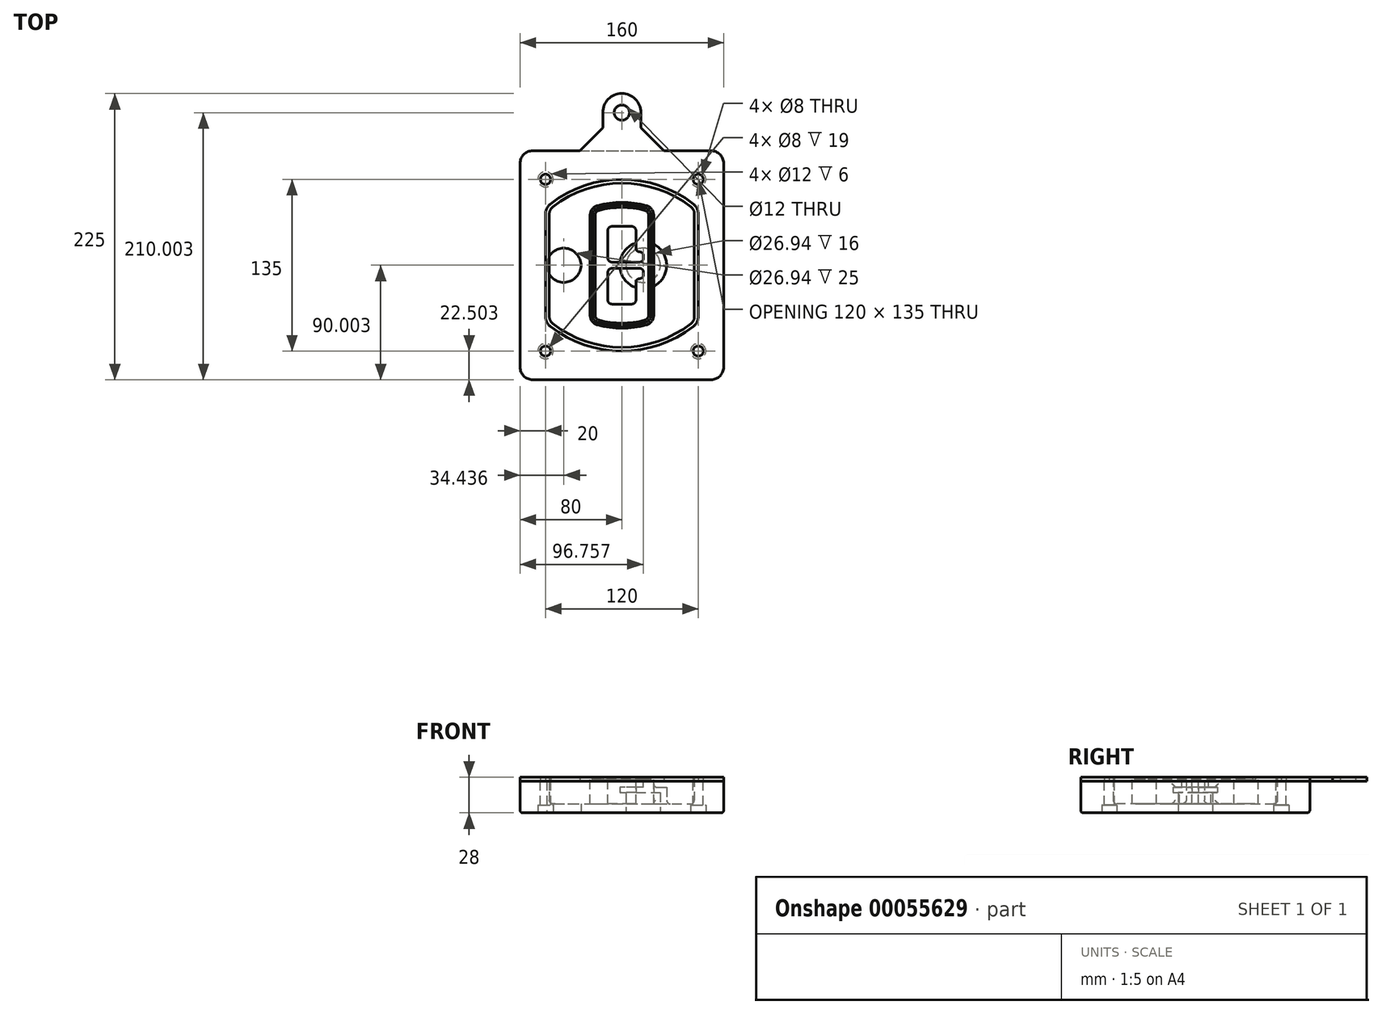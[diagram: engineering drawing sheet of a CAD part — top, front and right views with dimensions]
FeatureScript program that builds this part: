
annotation { "Feature Type Name" : "Feature", "Feature Type Description" : "" }
export const myFeature = defineFeature(function(context is Context, id is Id, definition is map)
    precondition{}
    {
        {
            var Q0;
            Q0=qCreatedBy(makeId("Top.planeOp"),FACE);
            var sketch = newSketch(context, id + "F0", { "sketchPlane" : qUnion([Q0])});
            skPoint(sketch, "E0.rect.middle", {"position": v(0, 0) * mm});
            skLineSegment(sketch, "E1.bottom", {"start": v(24.05, 28.38) * mm, "end": v(164.05, 28.38) * mm});
            skLineSegment(sketch, "E1.top", {"start": v(24.05, 208.38) * mm, "end": v(164.05, 208.38) * mm});
            skLineSegment(sketch, "E1.left", {"start": v(14.05, 38.38) * mm, "end": v(14.05, 198.38) * mm});
            skLineSegment(sketch, "E1.right", {"start": v(174.05, 38.38) * mm, "end": v(174.05, 198.38) * mm});
            skLineSegment(sketch, "E2", {"start": v(14.05, 208.38) * mm, "end": v(174.05, 28.38) * mm, "construction": true});
            skLineSegment(sketch, "E3", {"start": v(174.05, 208.38) * mm, "end": v(14.05, 28.38) * mm, "construction": true});
            skCircle(sketch, "E4", {"center": v(34.05, 185.88) * mm, "radius": 4 * mm});
            skCircle(sketch, "E5", {"center": v(154.05, 185.88) * mm, "radius": 4 * mm});
            skCircle(sketch, "E6", {"center": v(154.05, 50.88) * mm, "radius": 4 * mm});
            skCircle(sketch, "E7", {"center": v(34.05, 50.88) * mm, "radius": 4 * mm});
            skLineSegment(sketch, "E8", {"start": v(34.05, 185.88) * mm, "end": v(154.05, 185.88) * mm, "construction": true});
            skLineSegment(sketch, "E9", {"start": v(154.05, 185.88) * mm, "end": v(154.05, 50.88) * mm, "construction": true});
            skLineSegment(sketch, "E10", {"start": v(154.05, 50.88) * mm, "end": v(34.05, 50.88) * mm, "construction": true});
            skLineSegment(sketch, "E11", {"start": v(34.05, 50.88) * mm, "end": v(34.05, 185.88) * mm, "construction": true});
            skLineSegment(sketch, "E12", {"start": v(34.05, 158.68) * mm, "end": v(34.05, 78.09) * mm});
            skLineSegment(sketch, "E13", {"start": v(154.05, 158.68) * mm, "end": v(154.05, 78.09) * mm});
            skArc(sketch, "E14", {"start": v(150.2, 166.56) * mm, "mid": v(94.05, 185.88) * mm, "end": v(37.9, 166.56) * mm});
            skArc(sketch, "E15", {"start": v(37.9, 70.2) * mm, "mid": v(94.05, 50.88) * mm, "end": v(150.2, 70.2) * mm});
            skLineSegment(sketch, "E16", {"start": v(34.05, 118.38) * mm, "end": v(154.05, 118.38) * mm, "construction": true});
            skPoint(sketch, "E17.visualSharp", {"position": v(34.05, 73.38) * mm});
            skArc(sketch, "E17.filletArc", {"start": v(34.05, 78.09) * mm, "mid": v(35.06, 73.7) * mm, "end": v(37.9, 70.2) * mm});
            skPoint(sketch, "E18.visualSharp", {"position": v(34.05, 163.38) * mm});
            skArc(sketch, "E18.filletArc", {"start": v(37.9, 166.56) * mm, "mid": v(35.06, 163.06) * mm, "end": v(34.05, 158.68) * mm});
            skPoint(sketch, "E19.visualSharp", {"position": v(154.05, 163.38) * mm});
            skArc(sketch, "E19.filletArc", {"start": v(154.05, 158.68) * mm, "mid": v(153.04, 163.06) * mm, "end": v(150.2, 166.56) * mm});
            skPoint(sketch, "E20.visualSharp", {"position": v(154.05, 73.38) * mm});
            skArc(sketch, "E20.filletArc", {"start": v(150.2, 70.2) * mm, "mid": v(153.04, 73.7) * mm, "end": v(154.05, 78.09) * mm});
            skPoint(sketch, "E21.visualSharp", {"position": v(14.05, 208.38) * mm});
            skArc(sketch, "E21.filletArc", {"start": v(24.05, 208.38) * mm, "mid": v(16.98, 205.45) * mm, "end": v(14.05, 198.38) * mm});
            skPoint(sketch, "E22.visualSharp", {"position": v(174.05, 208.38) * mm});
            skArc(sketch, "E22.filletArc", {"start": v(174.05, 198.38) * mm, "mid": v(171.12, 205.45) * mm, "end": v(164.05, 208.38) * mm});
            skPoint(sketch, "E23.visualSharp", {"position": v(174.05, 28.38) * mm});
            skArc(sketch, "E23.filletArc", {"start": v(164.05, 28.38) * mm, "mid": v(171.12, 31.31) * mm, "end": v(174.05, 38.38) * mm});
            skPoint(sketch, "E24.visualSharp", {"position": v(14.05, 28.38) * mm});
            skArc(sketch, "E24.filletArc", {"start": v(14.05, 38.38) * mm, "mid": v(16.98, 31.31) * mm, "end": v(24.05, 28.38) * mm});
            skArc(sketch, "E25.0", {"start": v(151.05, 158.68) * mm, "mid": v(150.34, 161.75) * mm, "end": v(148.36, 164.2) * mm});
            skLineSegment(sketch, "E25.1", {"start": v(151.05, 158.68) * mm, "end": v(151.05, 78.09) * mm});
            skArc(sketch, "E25.2", {"start": v(148.36, 72.57) * mm, "mid": v(150.34, 75.02) * mm, "end": v(151.05, 78.09) * mm});
            skArc(sketch, "E25.3", {"start": v(39.74, 72.57) * mm, "mid": v(94.05, 53.88) * mm, "end": v(148.36, 72.57) * mm});
            skArc(sketch, "E25.4", {"start": v(37.05, 78.09) * mm, "mid": v(37.76, 75.02) * mm, "end": v(39.74, 72.57) * mm});
            skArc(sketch, "E25.5", {"start": v(148.36, 164.2) * mm, "mid": v(94.05, 182.88) * mm, "end": v(39.74, 164.2) * mm});
            skLineSegment(sketch, "E25.6", {"start": v(37.05, 158.68) * mm, "end": v(37.05, 78.09) * mm});
            skArc(sketch, "E25.7", {"start": v(39.74, 164.2) * mm, "mid": v(37.76, 161.75) * mm, "end": v(37.05, 158.68) * mm});
            skArc(sketch, "E26.0", {"start": v(35.43, 169.71) * mm, "mid": v(31.47, 164.82) * mm, "end": v(30.05, 158.68) * mm});
            skArc(sketch, "E26.1", {"start": v(152.67, 169.71) * mm, "mid": v(94.05, 189.88) * mm, "end": v(35.43, 169.71) * mm});
            skArc(sketch, "E26.2", {"start": v(158.05, 158.68) * mm, "mid": v(156.63, 164.82) * mm, "end": v(152.67, 169.71) * mm});
            skLineSegment(sketch, "E26.3", {"start": v(158.05, 158.68) * mm, "end": v(158.05, 78.09) * mm});
            skArc(sketch, "E26.4", {"start": v(152.67, 67.05) * mm, "mid": v(156.63, 71.95) * mm, "end": v(158.05, 78.09) * mm});
            skLineSegment(sketch, "E26.5", {"start": v(30.05, 158.68) * mm, "end": v(30.05, 78.09) * mm});
            skArc(sketch, "E26.6", {"start": v(35.43, 67.05) * mm, "mid": v(94.05, 46.88) * mm, "end": v(152.67, 67.05) * mm});
            skArc(sketch, "E26.7", {"start": v(30.05, 78.09) * mm, "mid": v(31.47, 71.95) * mm, "end": v(35.43, 67.05) * mm});
            skSolve(sketch);
        }
        {
            var Q0;
            Q0=makeQuery(id+"F0.imprint","IMPRINT",FACE,{"disambiguationData":[TD([[makeQuery(id+"F0.imprint","IMPRINT",EDGE,{"derivedFrom":sQuery(id+"F0.wireOp",EDGE,"E1.bottom")}),1.0]])]});
            var Q1;
            Q1=makeQuery(id+"F0.imprint","IMPRINT",FACE,{"disambiguationData":[TD([[makeQuery(id+"F0.imprint","IMPRINT",EDGE,{"derivedFrom":sQuery(id+"F0.wireOp",EDGE,"E12")}),1.0]])]});
            var Q2;
            Q2=makeQuery(id+"F0.imprint","IMPRINT",FACE,{"disambiguationData":[TD([[makeQuery(id+"F0.imprint","IMPRINT",EDGE,{"derivedFrom":sQuery(id+"F0.wireOp",EDGE,"E25.0")}),1.0]])]});
            var Q3;
            Q3=makeQuery(id+"F0.imprint","IMPRINT",FACE,{"disambiguationData":[TD([[makeQuery(id+"F0.imprint","IMPRINT",EDGE,{"derivedFrom":sQuery(id+"F0.wireOp",EDGE,"E12")}),-1.0]])]});
            extrude(context, id + "F1", {"entities" : qUnion([Q0, Q1, Q2, Q3]), "oppositeDirection" : true, "depth" : 25 * mm});
        }
        {
            var Q0;
            Q0=makeQuery(id+"F0.imprint","IMPRINT",FACE,{"disambiguationData":[TD([[makeQuery(id+"F0.imprint","IMPRINT",EDGE,{"derivedFrom":sQuery(id+"F0.wireOp",EDGE,"E12")}),1.0]])]});
            extrude(context, id + "F2", {"entities" : qUnion([Q0]), "operationType" : NewBodyOperationType.ADD, "depth" : 3 * mm});
        }
        {
            var Q0;
            Q0=makeQuery(id+"F0.imprint","IMPRINT",FACE,{"disambiguationData":[TD([[makeQuery(id+"F0.imprint","IMPRINT",EDGE,{"derivedFrom":sQuery(id+"F0.wireOp",EDGE,"E25.0")}),1.0]])]});
            extrude(context, id + "F3", {"entities" : qUnion([Q0]), "operationType" : NewBodyOperationType.REMOVE, "oppositeDirection" : true, "depth" : 18 * mm});
        }
        {
            var Q0;
            Q0=makeQuery(id+"F2.opExtrude","CAP_FACE",FACE,{"disambiguationData":[OSD([sQuery(id+"F0.wireOp",EDGE,"E12"),sQuery(id+"F0.wireOp",EDGE,"E13"),sQuery(id+"F0.wireOp",EDGE,"E14"),sQuery(id+"F0.wireOp",EDGE,"E15"),sQuery(id+"F0.wireOp",EDGE,"E17.filletArc"),sQuery(id+"F0.wireOp",EDGE,"E18.filletArc"),sQuery(id+"F0.wireOp",EDGE,"E19.filletArc"),sQuery(id+"F0.wireOp",EDGE,"E20.filletArc"),sQuery(id+"F0.wireOp",EDGE,"E25.0"),sQuery(id+"F0.wireOp",EDGE,"E25.1"),sQuery(id+"F0.wireOp",EDGE,"E25.2"),sQuery(id+"F0.wireOp",EDGE,"E25.3"),sQuery(id+"F0.wireOp",EDGE,"E25.4"),sQuery(id+"F0.wireOp",EDGE,"E25.5"),sQuery(id+"F0.wireOp",EDGE,"E25.6"),sQuery(id+"F0.wireOp",EDGE,"E25.7")])],"isStart":false});
            var sketch = newSketch(context, id + "F4", { "sketchPlane" : qUnion([Q0])});
            skArc(sketch, "E27.0", {"start": v(74.97, 71.41) * mm, "mid": v(94.05, 68.88) * mm, "end": v(113.13, 71.41) * mm});
            skArc(sketch, "E28.0", {"start": v(113.13, 165.35) * mm, "mid": v(94.05, 167.88) * mm, "end": v(74.97, 165.35) * mm});
            skLineSegment(sketch, "E29", {"start": v(69.05, 157.63) * mm, "end": v(69.05, 79.14) * mm});
            skLineSegment(sketch, "E30", {"start": v(119.05, 157.63) * mm, "end": v(119.05, 79.14) * mm});
            skLineSegment(sketch, "E31", {"start": v(69.05, 163.48) * mm, "end": v(119.05, 163.48) * mm, "construction": true});
            skLineSegment(sketch, "E32", {"start": v(69.05, 73.28) * mm, "end": v(119.05, 73.28) * mm, "construction": true});
            skPoint(sketch, "E33.visualSharp", {"position": v(69.05, 163.48) * mm});
            skArc(sketch, "E33.filletArc", {"start": v(74.97, 165.35) * mm, "mid": v(70.7, 162.5) * mm, "end": v(69.05, 157.63) * mm});
            skPoint(sketch, "E34.visualSharp", {"position": v(119.05, 163.48) * mm});
            skArc(sketch, "E34.filletArc", {"start": v(119.05, 157.63) * mm, "mid": v(117.4, 162.5) * mm, "end": v(113.13, 165.35) * mm});
            skPoint(sketch, "E35.visualSharp", {"position": v(119.05, 73.28) * mm});
            skArc(sketch, "E35.filletArc", {"start": v(113.13, 71.41) * mm, "mid": v(117.4, 74.27) * mm, "end": v(119.05, 79.14) * mm});
            skPoint(sketch, "E36.visualSharp", {"position": v(69.05, 73.28) * mm});
            skArc(sketch, "E36.filletArc", {"start": v(69.05, 79.14) * mm, "mid": v(70.7, 74.27) * mm, "end": v(74.97, 71.41) * mm});
            skArc(sketch, "E37.0", {"start": v(148.36, 164.2) * mm, "mid": v(94.05, 182.88) * mm, "end": v(39.74, 164.2) * mm});
            skArc(sketch, "E37.1", {"start": v(39.74, 164.2) * mm, "mid": v(37.76, 161.75) * mm, "end": v(37.05, 158.68) * mm});
            skLineSegment(sketch, "E37.2", {"start": v(37.05, 158.68) * mm, "end": v(37.05, 78.09) * mm});
            skArc(sketch, "E37.3", {"start": v(37.05, 78.09) * mm, "mid": v(37.76, 75.02) * mm, "end": v(39.74, 72.57) * mm});
            skArc(sketch, "E37.4", {"start": v(39.74, 72.57) * mm, "mid": v(94.05, 53.88) * mm, "end": v(148.36, 72.57) * mm});
            skArc(sketch, "E37.5", {"start": v(148.36, 72.57) * mm, "mid": v(150.34, 75.02) * mm, "end": v(151.05, 78.09) * mm});
            skLineSegment(sketch, "E37.6", {"start": v(151.05, 158.68) * mm, "end": v(151.05, 78.09) * mm});
            skArc(sketch, "E37.7", {"start": v(151.05, 158.68) * mm, "mid": v(150.34, 161.75) * mm, "end": v(148.36, 164.2) * mm});
            skLineSegment(sketch, "E38.0", {"start": v(117.05, 157.63) * mm, "end": v(117.05, 79.14) * mm});
            skArc(sketch, "E38.1", {"start": v(112.61, 73.34) * mm, "mid": v(115.81, 75.49) * mm, "end": v(117.05, 79.14) * mm});
            skArc(sketch, "E38.2", {"start": v(75.49, 73.34) * mm, "mid": v(94.05, 70.88) * mm, "end": v(112.61, 73.34) * mm});
            skArc(sketch, "E38.3", {"start": v(71.05, 79.14) * mm, "mid": v(72.29, 75.49) * mm, "end": v(75.49, 73.34) * mm});
            skLineSegment(sketch, "E38.4", {"start": v(71.05, 157.63) * mm, "end": v(71.05, 79.14) * mm});
            skArc(sketch, "E38.5", {"start": v(117.05, 157.63) * mm, "mid": v(115.81, 161.28) * mm, "end": v(112.61, 163.42) * mm});
            skArc(sketch, "E38.6", {"start": v(75.49, 163.42) * mm, "mid": v(72.29, 161.28) * mm, "end": v(71.05, 157.63) * mm});
            skArc(sketch, "E38.7", {"start": v(112.61, 163.42) * mm, "mid": v(94.05, 165.88) * mm, "end": v(75.49, 163.42) * mm});
            skArc(sketch, "E39.0", {"start": v(115.05, 157.63) * mm, "mid": v(114.23, 160.06) * mm, "end": v(112.1, 161.5) * mm});
            skLineSegment(sketch, "E39.1", {"start": v(115.05, 157.63) * mm, "end": v(115.05, 79.14) * mm});
            skArc(sketch, "E39.2", {"start": v(112.1, 75.27) * mm, "mid": v(114.23, 76.7) * mm, "end": v(115.05, 79.14) * mm});
            skArc(sketch, "E39.3", {"start": v(76, 75.27) * mm, "mid": v(94.05, 72.88) * mm, "end": v(112.1, 75.27) * mm});
            skArc(sketch, "E39.4", {"start": v(73.05, 79.14) * mm, "mid": v(73.87, 76.7) * mm, "end": v(76, 75.27) * mm});
            skArc(sketch, "E39.5", {"start": v(112.1, 161.5) * mm, "mid": v(94.05, 163.88) * mm, "end": v(76, 161.5) * mm});
            skLineSegment(sketch, "E39.6", {"start": v(73.05, 157.63) * mm, "end": v(73.05, 79.14) * mm});
            skArc(sketch, "E39.7", {"start": v(76, 161.5) * mm, "mid": v(73.87, 160.06) * mm, "end": v(73.05, 157.63) * mm});
            skLineSegment(sketch, "E40", {"start": v(69.05, 118.38) * mm, "end": v(119.05, 118.38) * mm, "construction": true});
            skLineSegment(sketch, "E41", {"start": v(83.05, 123.88) * mm, "end": v(83.05, 145.88) * mm});
            skLineSegment(sketch, "E42", {"start": v(86.05, 148.88) * mm, "end": v(102.05, 148.88) * mm});
            skLineSegment(sketch, "E43", {"start": v(105.05, 145.88) * mm, "end": v(105.05, 131.88) * mm});
            skLineSegment(sketch, "E44", {"start": v(108.05, 128.88) * mm, "end": v(108.05, 128.88) * mm});
            skLineSegment(sketch, "E45", {"start": v(111.05, 125.88) * mm, "end": v(111.05, 123.88) * mm});
            skLineSegment(sketch, "E46", {"start": v(108.05, 120.88) * mm, "end": v(86.05, 120.88) * mm});
            skPoint(sketch, "E47.visualSharp", {"position": v(83.05, 148.88) * mm});
            skArc(sketch, "E47.filletArc", {"start": v(86.05, 148.88) * mm, "mid": v(83.93, 148) * mm, "end": v(83.05, 145.88) * mm});
            skPoint(sketch, "E48.visualSharp", {"position": v(105.05, 148.88) * mm});
            skArc(sketch, "E48.filletArc", {"start": v(105.05, 145.88) * mm, "mid": v(104.17, 148) * mm, "end": v(102.05, 148.88) * mm});
            skPoint(sketch, "E49.visualSharp", {"position": v(105.05, 128.88) * mm});
            skArc(sketch, "E49.filletArc", {"start": v(105.05, 131.88) * mm, "mid": v(105.93, 129.76) * mm, "end": v(108.05, 128.88) * mm});
            skPoint(sketch, "E50.visualSharp", {"position": v(111.05, 128.88) * mm});
            skArc(sketch, "E50.filletArc", {"start": v(111.05, 125.88) * mm, "mid": v(110.17, 128) * mm, "end": v(108.05, 128.88) * mm});
            skPoint(sketch, "E51.visualSharp", {"position": v(111.05, 120.88) * mm});
            skArc(sketch, "E51.filletArc", {"start": v(108.05, 120.88) * mm, "mid": v(110.17, 121.76) * mm, "end": v(111.05, 123.88) * mm});
            skPoint(sketch, "E52.visualSharp", {"position": v(83.05, 120.88) * mm});
            skArc(sketch, "E52.filletArc", {"start": v(83.05, 123.88) * mm, "mid": v(83.93, 121.76) * mm, "end": v(86.05, 120.88) * mm});
            skLineSegment(sketch, "E53.0.MirrorCS", {"start": v(108.05, 115.88) * mm, "end": v(86.05, 115.88) * mm});
            skArc(sketch, "E54.0.MirrorCS", {"start": v(83.05, 112.88) * mm, "mid": v(83.93, 115) * mm, "end": v(86.05, 115.88) * mm});
            skLineSegment(sketch, "E55.0.MirrorCS", {"start": v(83.05, 112.88) * mm, "end": v(83.05, 90.88) * mm});
            skArc(sketch, "E56.0.MirrorCS", {"start": v(86.05, 87.88) * mm, "mid": v(83.93, 88.76) * mm, "end": v(83.05, 90.88) * mm});
            skLineSegment(sketch, "E57.0.MirrorCS", {"start": v(86.05, 87.88) * mm, "end": v(102.05, 87.88) * mm});
            skArc(sketch, "E58.0.MirrorCS", {"start": v(105.05, 90.88) * mm, "mid": v(104.17, 88.76) * mm, "end": v(102.05, 87.88) * mm});
            skLineSegment(sketch, "E59.0.MirrorCS", {"start": v(105.05, 90.88) * mm, "end": v(105.05, 104.88) * mm});
            skArc(sketch, "E60.0.MirrorCS", {"start": v(105.05, 104.88) * mm, "mid": v(105.93, 107) * mm, "end": v(108.05, 107.88) * mm});
            skArc(sketch, "E61.0.MirrorCS", {"start": v(111.05, 110.88) * mm, "mid": v(110.17, 108.76) * mm, "end": v(108.05, 107.88) * mm});
            skLineSegment(sketch, "E62.0.MirrorCS", {"start": v(111.05, 110.88) * mm, "end": v(111.05, 112.88) * mm});
            skArc(sketch, "E63.0.MirrorCS", {"start": v(108.05, 115.88) * mm, "mid": v(110.17, 115) * mm, "end": v(111.05, 112.88) * mm});
            skSolve(sketch);
        }
        {
            var Q0;
            Q0=makeQuery(id+"F4.imprint","IMPRINT",FACE,{"disambiguationData":[TD([[makeQuery(id+"F4.imprint","IMPRINT",EDGE,{"derivedFrom":sQuery(id+"F4.wireOp",EDGE,"E27.0")}),1.0]])]});
            var Q1;
            Q1=makeQuery(id+"F4.imprint","IMPRINT",FACE,{"disambiguationData":[TD([[makeQuery(id+"F4.imprint","IMPRINT",EDGE,{"derivedFrom":sQuery(id+"F4.wireOp",EDGE,"E38.0")}),-1.0]])]});
            var Q2;
            Q2=makeQuery(id+"F4.imprint","IMPRINT",FACE,{"disambiguationData":[TD([[makeQuery(id+"F4.imprint","IMPRINT",EDGE,{"derivedFrom":sQuery(id+"F4.wireOp",EDGE,"E39.0")}),1.0]])]});
            extrude(context, id + "F5", {"entities" : qUnion([Q0, Q1, Q2]), "operationType" : NewBodyOperationType.ADD, "endBound" : BoundingType.UP_TO_NEXT, "oppositeDirection" : true, "depth" : 25 * mm});
        }
        {
            var Q0;
            Q0=makeQuery(id+"F4.imprint","IMPRINT",FACE,{"disambiguationData":[TD([[makeQuery(id+"F4.imprint","IMPRINT",EDGE,{"derivedFrom":sQuery(id+"F4.wireOp",EDGE,"E38.0")}),-1.0]])]});
            extrude(context, id + "F6", {"entities" : qUnion([Q0]), "operationType" : NewBodyOperationType.REMOVE, "oppositeDirection" : true, "depth" : 2 * mm});
        }
        {
            var Q0;
            Q0=makeQuery(id+"F1.opExtrude","CAP_FACE",FACE,{"disambiguationData":[OSD([sQuery(id+"F0.wireOp",EDGE,"E1.bottom"),sQuery(id+"F0.wireOp",EDGE,"E1.top"),sQuery(id+"F0.wireOp",EDGE,"E1.left"),sQuery(id+"F0.wireOp",EDGE,"E1.right"),sQuery(id+"F0.wireOp",EDGE,"E4"),sQuery(id+"F0.wireOp",EDGE,"E5"),sQuery(id+"F0.wireOp",EDGE,"E6"),sQuery(id+"F0.wireOp",EDGE,"E7"),sQuery(id+"F0.wireOp",EDGE,"E21.filletArc"),sQuery(id+"F0.wireOp",EDGE,"E22.filletArc"),sQuery(id+"F0.wireOp",EDGE,"E23.filletArc"),sQuery(id+"F0.wireOp",EDGE,"E24.filletArc")])],"isStart":false});
            var sketch = newSketch(context, id + "F7", { "sketchPlane" : qUnion([Q0])});
            skCircle(sketch, "E64", {"center": v(110.8, -118.38) * mm, "radius": 13.47 * mm});
            skCircle(sketch, "E65", {"center": v(48.49, -118.38) * mm, "radius": 13.47 * mm});
            skLineSegment(sketch, "E66", {"start": v(174.05, -118.38) * mm, "end": v(14.05, -118.38) * mm});
            skCircle(sketch, "E67", {"center": v(110.8, -118.38) * mm, "radius": 18.47 * mm});
            skCircle(sketch, "E68", {"center": v(154.05, -185.88) * mm, "radius": 6 * mm});
            skCircle(sketch, "E69", {"center": v(34.05, -185.88) * mm, "radius": 6 * mm});
            skCircle(sketch, "E70", {"center": v(34.05, -50.88) * mm, "radius": 6 * mm});
            skCircle(sketch, "E71", {"center": v(154.05, -50.88) * mm, "radius": 6 * mm});
            skSolve(sketch);
        }
        {
            var Q0;
            {var subQ1=sQuery(id+"F7.wireOp",EDGE,"E66");var subQ4=sQuery(id+"F7.wireOp",EDGE,"E64");var subQ6=makeQuery(id+"F7.imprint","INTERSECT",VERTEX,{"disambiguationData":[OD(0.0)],"derivedFrom":[subQ4,subQ1]});Q0=makeQuery(id+"F7.imprint","IMPRINT",FACE,{"disambiguationData":[TD([[makeQuery(id+"F7.imprint","IMPRINT",EDGE,{"disambiguationData":[TD([[subQ6,-1.0]])],"derivedFrom":subQ4}),-1.0]])]});}
            var Q1;
            {var subQ0=sQuery(id+"F7.wireOp",EDGE,"E66");var subQ1=sQuery(id+"F7.wireOp",EDGE,"E64");var subQ3=makeQuery(id+"F7.imprint","INTERSECT",VERTEX,{"disambiguationData":[OD(0.0)],"derivedFrom":[subQ1,subQ0]});Q1=makeQuery(id+"F7.imprint","IMPRINT",FACE,{"disambiguationData":[TD([[makeQuery(id+"F7.imprint","IMPRINT",EDGE,{"disambiguationData":[TD([[subQ3,-1.0]])],"derivedFrom":subQ1}),1.0]])]});}
            var Q2;
            {var subQ0=sQuery(id+"F7.wireOp",EDGE,"E66");var subQ1=sQuery(id+"F7.wireOp",EDGE,"E64");var subQ3=makeQuery(id+"F7.imprint","INTERSECT",VERTEX,{"disambiguationData":[OD(0.0)],"derivedFrom":[subQ1,subQ0]});Q2=makeQuery(id+"F7.imprint","IMPRINT",FACE,{"disambiguationData":[TD([[makeQuery(id+"F7.imprint","IMPRINT",EDGE,{"disambiguationData":[TD([[subQ3,1.0]])],"derivedFrom":subQ1}),1.0]])]});}
            var Q3;
            {var subQ1=sQuery(id+"F7.wireOp",EDGE,"E66");var subQ4=sQuery(id+"F7.wireOp",EDGE,"E64");var subQ6=makeQuery(id+"F7.imprint","INTERSECT",VERTEX,{"disambiguationData":[OD(0.0)],"derivedFrom":[subQ4,subQ1]});Q3=makeQuery(id+"F7.imprint","IMPRINT",FACE,{"disambiguationData":[TD([[makeQuery(id+"F7.imprint","IMPRINT",EDGE,{"disambiguationData":[TD([[subQ6,1.0]])],"derivedFrom":subQ4}),-1.0]])]});}
            extrude(context, id + "F8", {"entities" : qUnion([Q0, Q1, Q2, Q3]), "operationType" : NewBodyOperationType.ADD, "oppositeDirection" : true, "depth" : 20 * mm});
        }
        {
            var Q0;
            {var subQ0=sQuery(id+"F7.wireOp",EDGE,"E66");var subQ1=sQuery(id+"F7.wireOp",EDGE,"E64");var subQ3=makeQuery(id+"F7.imprint","INTERSECT",VERTEX,{"disambiguationData":[OD(0.0)],"derivedFrom":[subQ1,subQ0]});Q0=makeQuery(id+"F7.imprint","IMPRINT",FACE,{"disambiguationData":[TD([[makeQuery(id+"F7.imprint","IMPRINT",EDGE,{"disambiguationData":[TD([[subQ3,-1.0]])],"derivedFrom":subQ1}),1.0]])]});}
            var Q1;
            {var subQ0=sQuery(id+"F7.wireOp",EDGE,"E66");var subQ1=sQuery(id+"F7.wireOp",EDGE,"E64");var subQ3=makeQuery(id+"F7.imprint","INTERSECT",VERTEX,{"disambiguationData":[OD(0.0)],"derivedFrom":[subQ1,subQ0]});Q1=makeQuery(id+"F7.imprint","IMPRINT",FACE,{"disambiguationData":[TD([[makeQuery(id+"F7.imprint","IMPRINT",EDGE,{"disambiguationData":[TD([[subQ3,1.0]])],"derivedFrom":subQ1}),1.0]])]});}
            extrude(context, id + "F9", {"entities" : qUnion([Q0, Q1]), "operationType" : NewBodyOperationType.REMOVE, "oppositeDirection" : true, "depth" : 16 * mm});
        }
        {
            var Q0;
            {var subQ0=sQuery(id+"F7.wireOp",EDGE,"E66");var subQ1=sQuery(id+"F7.wireOp",EDGE,"E65");var subQ3=makeQuery(id+"F7.imprint","INTERSECT",VERTEX,{"disambiguationData":[OD(0.0)],"derivedFrom":[subQ1,subQ0]});Q0=makeQuery(id+"F7.imprint","IMPRINT",FACE,{"disambiguationData":[TD([[makeQuery(id+"F7.imprint","IMPRINT",EDGE,{"disambiguationData":[TD([[subQ3,-1.0]])],"derivedFrom":subQ1}),1.0]])]});}
            var Q1;
            {var subQ0=sQuery(id+"F7.wireOp",EDGE,"E66");var subQ1=sQuery(id+"F7.wireOp",EDGE,"E65");var subQ3=makeQuery(id+"F7.imprint","INTERSECT",VERTEX,{"disambiguationData":[OD(0.0)],"derivedFrom":[subQ1,subQ0]});Q1=makeQuery(id+"F7.imprint","IMPRINT",FACE,{"disambiguationData":[TD([[makeQuery(id+"F7.imprint","IMPRINT",EDGE,{"disambiguationData":[TD([[subQ3,1.0]])],"derivedFrom":subQ1}),1.0]])]});}
            extrude(context, id + "F10", {"entities" : qUnion([Q0, Q1]), "operationType" : NewBodyOperationType.REMOVE, "oppositeDirection" : true, "depth" : 25 * mm});
        }
        {
            var Q0;
            Q0=makeQuery(id+"F7.imprint","IMPRINT",FACE,{"disambiguationData":[TD([[makeQuery(id+"F7.imprint","IMPRINT",EDGE,{"derivedFrom":sQuery(id+"F7.wireOp",EDGE,"E68")}),1.0]])]});
            var Q1;
            Q1=makeQuery(id+"F7.imprint","IMPRINT",FACE,{"disambiguationData":[TD([[makeQuery(id+"F7.imprint","IMPRINT",EDGE,{"derivedFrom":makeQuery(id+"F1.opExtrude","CAP_EDGE",EDGE,{"disambiguationData":[OSD([sQuery(id+"F0.wireOp",EDGE,"E5")])],"isStart":false})}),-1.0]])]});
            var Q2;
            Q2=makeQuery(id+"F7.imprint","IMPRINT",FACE,{"disambiguationData":[TD([[makeQuery(id+"F7.imprint","IMPRINT",EDGE,{"derivedFrom":sQuery(id+"F7.wireOp",EDGE,"E69")}),1.0]])]});
            var Q3;
            Q3=makeQuery(id+"F7.imprint","IMPRINT",FACE,{"disambiguationData":[TD([[makeQuery(id+"F7.imprint","IMPRINT",EDGE,{"derivedFrom":makeQuery(id+"F1.opExtrude","CAP_EDGE",EDGE,{"disambiguationData":[OSD([sQuery(id+"F0.wireOp",EDGE,"E4")])],"isStart":false})}),-1.0]])]});
            var Q4;
            Q4=makeQuery(id+"F7.imprint","IMPRINT",FACE,{"disambiguationData":[TD([[makeQuery(id+"F7.imprint","IMPRINT",EDGE,{"derivedFrom":sQuery(id+"F7.wireOp",EDGE,"E70")}),1.0]])]});
            var Q5;
            Q5=makeQuery(id+"F7.imprint","IMPRINT",FACE,{"disambiguationData":[TD([[makeQuery(id+"F7.imprint","IMPRINT",EDGE,{"derivedFrom":makeQuery(id+"F1.opExtrude","CAP_EDGE",EDGE,{"disambiguationData":[OSD([sQuery(id+"F0.wireOp",EDGE,"E7")])],"isStart":false})}),-1.0]])]});
            var Q6;
            Q6=makeQuery(id+"F7.imprint","IMPRINT",FACE,{"disambiguationData":[TD([[makeQuery(id+"F7.imprint","IMPRINT",EDGE,{"derivedFrom":sQuery(id+"F7.wireOp",EDGE,"E71")}),1.0]])]});
            var Q7;
            Q7=makeQuery(id+"F7.imprint","IMPRINT",FACE,{"disambiguationData":[TD([[makeQuery(id+"F7.imprint","IMPRINT",EDGE,{"derivedFrom":makeQuery(id+"F1.opExtrude","CAP_EDGE",EDGE,{"disambiguationData":[OSD([sQuery(id+"F0.wireOp",EDGE,"E6")])],"isStart":false})}),-1.0]])]});
            extrude(context, id + "F11", {"entities" : qUnion([Q0, Q1, Q2, Q3, Q4, Q5, Q6, Q7]), "operationType" : NewBodyOperationType.REMOVE, "oppositeDirection" : true, "depth" : 6 * mm});
        }
        {
            var Q0;
            Q0=makeQuery(id+"F9.boolean.opBoolean","COPY",FACE,{"derivedFrom":makeQuery(id+"F9.opExtrude","CAP_FACE",FACE,{"disambiguationData":[OSD([sQuery(id+"F7.wireOp",EDGE,"E64")])],"isStart":false})});
            var sketch = newSketch(context, id + "F12", { "sketchPlane" : qUnion([Q0])});
            skArc(sketch, "E72.0", {"start": v(105.05, -100.83) * mm, "mid": v(96.62, -106.56) * mm, "end": v(92.5, -115.88) * mm});
            skArc(sketch, "E72.1", {"start": v(92.5, -120.88) * mm, "mid": v(96.62, -130.2) * mm, "end": v(105.05, -135.93) * mm});
            skLineSegment(sketch, "E73", {"start": v(92.5, -120.88) * mm, "end": v(108.05, -120.88) * mm});
            skLineSegment(sketch, "E74.0", {"start": v(108.05, -115.88) * mm, "end": v(92.5, -115.88) * mm});
            skArc(sketch, "E74.1", {"start": v(108.05, -115.88) * mm, "mid": v(110.17, -115) * mm, "end": v(111.05, -112.88) * mm});
            skLineSegment(sketch, "E74.2", {"start": v(111.05, -110.88) * mm, "end": v(111.05, -112.88) * mm});
            skArc(sketch, "E74.3", {"start": v(111.05, -110.88) * mm, "mid": v(110.17, -108.76) * mm, "end": v(108.05, -107.88) * mm});
            skArc(sketch, "E74.4", {"start": v(105.05, -104.88) * mm, "mid": v(105.93, -107) * mm, "end": v(108.05, -107.88) * mm});
            skLineSegment(sketch, "E74.5", {"start": v(105.05, -100.83) * mm, "end": v(105.05, -104.88) * mm});
            skLineSegment(sketch, "E74.7", {"start": v(108.05, -120.88) * mm, "end": v(92.5, -120.88) * mm});
            skArc(sketch, "E74.8", {"start": v(108.05, -120.88) * mm, "mid": v(110.17, -121.76) * mm, "end": v(111.05, -123.88) * mm});
            skLineSegment(sketch, "E74.9", {"start": v(111.05, -125.88) * mm, "end": v(111.05, -123.88) * mm});
            skArc(sketch, "E74.10", {"start": v(111.05, -125.88) * mm, "mid": v(110.17, -128) * mm, "end": v(108.05, -128.88) * mm});
            skArc(sketch, "E74.11", {"start": v(105.05, -131.88) * mm, "mid": v(105.93, -129.76) * mm, "end": v(108.05, -128.88) * mm});
            skLineSegment(sketch, "E74.12", {"start": v(105.05, -135.93) * mm, "end": v(105.05, -131.88) * mm});
            skPoint(sketch, "E75.orphan", {"position": v(105.05, -145.88) * mm});
            skPoint(sketch, "E76.orphan", {"position": v(86.05, -120.88) * mm});
            skPoint(sketch, "E77.orphan", {"position": v(86.05, -115.88) * mm});
            skPoint(sketch, "E78.orphan", {"position": v(105.05, -90.88) * mm});
            skSolve(sketch);
        }
        {
            var Q0;
            {var subQ7=sQuery(id+"F12.wireOp",EDGE,"E72.0");var subQ14=sQuery(id+"F12.wireOp",EDGE,"E72.1");var subQ16=sQuery(id+"F12.wireOp",EDGE,"E74.1");var subQ18=sQuery(id+"F12.wireOp",EDGE,"E74.8");Q0=qUnion([makeQuery(id+"F12.imprint","IMPRINT",FACE,{"disambiguationData":[TD([[makeQuery(id+"F12.imprint","IMPRINT",EDGE,{"derivedFrom":subQ7}),1.0]])]}),makeQuery(id+"F12.imprint","IMPRINT",FACE,{"disambiguationData":[TD([[makeQuery(id+"F12.imprint","IMPRINT",EDGE,{"derivedFrom":subQ14}),1.0]])]}),makeQuery(id+"F12.imprint","IMPRINT",FACE,{"disambiguationData":[TD([[makeQuery(id+"F12.imprint","IMPRINT",EDGE,{"derivedFrom":subQ16}),1.0]])]}),makeQuery(id+"F12.imprint","IMPRINT",FACE,{"disambiguationData":[TD([[makeQuery(id+"F12.imprint","IMPRINT",EDGE,{"derivedFrom":subQ18}),-1.0]])]})]);}
            var Q1;
            Q1=makeQuery(id+"F5.boolean.opBoolean","SPLIT",FACE,{"disambiguationData":[TD([makeQuery(id+"F5.opExtrude","SWEPT_FACE",FACE,{"disambiguationData":[OSD([sQuery(id+"F4.wireOp",EDGE,"E41")])]})])],"derivedFrom":makeQuery(id+"F3.boolean.opBoolean","COPY",FACE,{"derivedFrom":makeQuery(id+"F3.opExtrude","CAP_FACE",FACE,{"disambiguationData":[OSD([sQuery(id+"F0.wireOp",EDGE,"E25.0"),sQuery(id+"F0.wireOp",EDGE,"E25.1"),sQuery(id+"F0.wireOp",EDGE,"E25.2"),sQuery(id+"F0.wireOp",EDGE,"E25.3"),sQuery(id+"F0.wireOp",EDGE,"E25.4"),sQuery(id+"F0.wireOp",EDGE,"E25.5"),sQuery(id+"F0.wireOp",EDGE,"E25.6"),sQuery(id+"F0.wireOp",EDGE,"E25.7")])],"isStart":false})})});
            extrude(context, id + "F13", {"entities" : qUnion([Q0]), "operationType" : NewBodyOperationType.REMOVE, "endBound" : BoundingType.UP_TO_SURFACE, "endBoundEntityFace" : qUnion([Q1]), "depth" : 25 * mm});
        }
        {
            var Q0;
            Q0=makeQuery(id+"F3.boolean.opBoolean","COPY",EDGE,{"derivedFrom":makeQuery(id+"F3.opExtrude","CAP_EDGE",EDGE,{"disambiguationData":[OSD([sQuery(id+"F0.wireOp",EDGE,"E25.6")])],"isStart":false})});
            var Q1;
            Q1=makeQuery(id+"F8.boolean.opBoolean","INTERSECT",EDGE,{"derivedFrom":[makeQuery(id+"F5.opExtrude","SWEPT_FACE",FACE,{"disambiguationData":[OSD([sQuery(id+"F4.wireOp",EDGE,"E30")])]}),makeQuery(id+"F8.opExtrude","CAP_FACE",FACE,{"disambiguationData":[OSD([sQuery(id+"F7.wireOp",EDGE,"E67")])],"isStart":false})]});
            var Q2;
            Q2=makeQuery(id+"F8.boolean.opBoolean","INTERSECT",EDGE,{"disambiguationData":[OD(1.0)],"derivedFrom":[makeQuery(id+"F5.opExtrude","SWEPT_FACE",FACE,{"disambiguationData":[OSD([sQuery(id+"F4.wireOp",EDGE,"E30")])]}),makeQuery(id+"F8.opExtrude","SWEPT_FACE",FACE,{"disambiguationData":[OSD([sQuery(id+"F7.wireOp",EDGE,"E67")])]})]});
            var Q3;
            {var subQ0=makeQuery(id+"F3.boolean.opBoolean","COPY",FACE,{"derivedFrom":makeQuery(id+"F3.opExtrude","CAP_FACE",FACE,{"disambiguationData":[OSD([sQuery(id+"F0.wireOp",EDGE,"E25.0"),sQuery(id+"F0.wireOp",EDGE,"E25.1"),sQuery(id+"F0.wireOp",EDGE,"E25.2"),sQuery(id+"F0.wireOp",EDGE,"E25.3"),sQuery(id+"F0.wireOp",EDGE,"E25.4"),sQuery(id+"F0.wireOp",EDGE,"E25.5"),sQuery(id+"F0.wireOp",EDGE,"E25.6"),sQuery(id+"F0.wireOp",EDGE,"E25.7")])],"isStart":false})});var subQ1=sQuery(id+"F4.wireOp",EDGE,"E30");Q3=makeQuery(id+"F8.boolean.opBoolean","SPLIT",EDGE,{"disambiguationData":[TD([makeQuery(id+"F5.opExtrude","SWEPT_FACE",FACE,{"disambiguationData":[OSD([sQuery(id+"F4.wireOp",EDGE,"E35.filletArc")])]})])],"derivedFrom":makeQuery(id+"F5.opExtrude","TWEAK_EDGE",EDGE,{"derivedFrom":[subQ0,makeQuery(id+"F4.imprint","IMPRINT",EDGE,{"derivedFrom":subQ1})]})});}
            var Q4;
            {var subQ0=sQuery(id+"F0.wireOp",EDGE,"E25.0");var subQ1=sQuery(id+"F0.wireOp",EDGE,"E25.1");var subQ2=sQuery(id+"F0.wireOp",EDGE,"E25.2");var subQ3=sQuery(id+"F0.wireOp",EDGE,"E25.3");var subQ4=sQuery(id+"F0.wireOp",EDGE,"E25.4");var subQ5=sQuery(id+"F0.wireOp",EDGE,"E25.5");var subQ6=sQuery(id+"F0.wireOp",EDGE,"E25.6");var subQ7=sQuery(id+"F0.wireOp",EDGE,"E25.7");Q4=makeQuery(id+"F8.boolean.opBoolean","INTERSECT",EDGE,{"derivedFrom":[makeQuery(id+"F5.boolean.opBoolean","SPLIT",FACE,{"disambiguationData":[TD([makeQuery(id+"F2.opExtrude","SWEPT_FACE",FACE,{"disambiguationData":[OSD([subQ0])]})])],"derivedFrom":makeQuery(id+"F3.boolean.opBoolean","COPY",FACE,{"derivedFrom":makeQuery(id+"F3.opExtrude","CAP_FACE",FACE,{"disambiguationData":[OSD([subQ0,subQ1,subQ2,subQ3,subQ4,subQ5,subQ6,subQ7])],"isStart":false})})}),makeQuery(id+"F8.opExtrude","SWEPT_FACE",FACE,{"disambiguationData":[OSD([sQuery(id+"F7.wireOp",EDGE,"E67")])]})]});}
            var Q5;
            Q5=makeQuery(id+"F8.boolean.opBoolean","INTERSECT",EDGE,{"disambiguationData":[OD(0.0)],"derivedFrom":[makeQuery(id+"F5.opExtrude","SWEPT_FACE",FACE,{"disambiguationData":[OSD([sQuery(id+"F4.wireOp",EDGE,"E30")])]}),makeQuery(id+"F8.opExtrude","SWEPT_FACE",FACE,{"disambiguationData":[OSD([sQuery(id+"F7.wireOp",EDGE,"E67")])]})]});
            fillet(context, id + "F14", {"entities" : qUnion([Q0, Q1, Q2, Q3, Q4, Q5]), "radius" : 3 * mm, "tangentPropagation" : true, "allowEdgeOverflow" : false});
        }
        {
            var Q0;
            Q0=makeQuery(id+"F1.opExtrude","CAP_EDGE",EDGE,{"disambiguationData":[OSD([sQuery(id+"F0.wireOp",EDGE,"E1.bottom")])],"isStart":false});
            fillet(context, id + "F15", {"entities" : qUnion([Q0]), "radius" : 2 * mm, "tangentPropagation" : true, "allowEdgeOverflow" : false});
        }
        {
            var Q0;
            {var subQ0=sQuery(id+"F0.wireOp",EDGE,"E22.filletArc");var subQ1=sQuery(id+"F0.wireOp",EDGE,"E7");var subQ2=sQuery(id+"F0.wireOp",EDGE,"E6");var subQ3=sQuery(id+"F0.wireOp",EDGE,"E5");var subQ4=sQuery(id+"F0.wireOp",EDGE,"E4");var subQ5=sQuery(id+"F0.wireOp",EDGE,"E1.bottom");var subQ6=sQuery(id+"F0.wireOp",EDGE,"E21.filletArc");var subQ7=sQuery(id+"F0.wireOp",EDGE,"E1.top");var subQ8=sQuery(id+"F0.wireOp",EDGE,"E1.left");var subQ9=sQuery(id+"F0.wireOp",EDGE,"E1.right");var subQ10=sQuery(id+"F0.wireOp",EDGE,"E23.filletArc");var subQ11=sQuery(id+"F0.wireOp",EDGE,"E24.filletArc");Q0=makeQuery(id+"F2.boolean.opBoolean","SPLIT",FACE,{"disambiguationData":[TD([makeQuery(id+"F1.opExtrude","SWEPT_FACE",FACE,{"disambiguationData":[OSD([subQ5])]})])],"derivedFrom":makeQuery(id+"F1.opExtrude","CAP_FACE",FACE,{"disambiguationData":[OSD([subQ5,subQ7,subQ8,subQ9,subQ4,subQ3,subQ2,subQ1,subQ6,subQ0,subQ10,subQ11])],"isStart":true})});}
            var sketch = newSketch(context, id + "F16", { "sketchPlane" : qUnion([Q0])});
            skLineSegment(sketch, "E79", {"start": v(94.05, 208.38) * mm, "end": v(94.05, 238.38) * mm, "construction": true});
            skCircle(sketch, "E80", {"center": v(94.05, 238.38) * mm, "radius": 6 * mm});
            skArc(sketch, "E81", {"start": v(109.05, 238.38) * mm, "mid": v(94.05, 253.38) * mm, "end": v(79.05, 238.38) * mm});
            skLineSegment(sketch, "E82", {"start": v(109.05, 238.38) * mm, "end": v(109.05, 226.38) * mm});
            skLineSegment(sketch, "E83", {"start": v(109.05, 226.38) * mm, "end": v(127.05, 208.38) * mm});
            skLineSegment(sketch, "E84", {"start": v(79.05, 238.38) * mm, "end": v(79.05, 226.38) * mm});
            skLineSegment(sketch, "E85", {"start": v(79.05, 226.38) * mm, "end": v(61.05, 208.38) * mm});
            skLineSegment(sketch, "E86", {"start": v(14.05, 118.38) * mm, "end": v(174.05, 118.38) * mm, "construction": true});
            skArc(sketch, "E87.MirrorCS", {"start": v(109.05, -1.62) * mm, "mid": v(94.05, -16.62) * mm, "end": v(79.05, -1.62) * mm});
            skCircle(sketch, "E88.MirrorC", {"center": v(94.05, -1.62) * mm, "radius": 6 * mm});
            skLineSegment(sketch, "E89.MirrorCS", {"start": v(109.05, -1.62) * mm, "end": v(109.05, 10.38) * mm});
            skLineSegment(sketch, "E90.MirrorCS", {"start": v(79.05, -1.62) * mm, "end": v(79.05, 10.38) * mm});
            skLineSegment(sketch, "E91.MirrorCS", {"start": v(94.05, 28.38) * mm, "end": v(94.05, -1.62) * mm, "construction": true});
            skLineSegment(sketch, "E92.MirrorCS", {"start": v(79.05, 10.38) * mm, "end": v(61.05, 28.38) * mm});
            skLineSegment(sketch, "E93.MirrorCS", {"start": v(109.05, 10.38) * mm, "end": v(127.05, 28.38) * mm});
            skSolve(sketch);
        }
        {
            var Q0;
            Q0=makeQuery(id+"F16.imprint","IMPRINT",FACE,{"disambiguationData":[TD([[makeQuery(id+"F16.imprint","IMPRINT",EDGE,{"derivedFrom":sQuery(id+"F16.wireOp",EDGE,"E80")}),-1.0]])]});
            var Q1;
            Q1=makeQuery(id+"F16.imprint","IMPRINT",FACE,{"disambiguationData":[TD([[makeQuery(id+"F16.imprint","IMPRINT",EDGE,{"derivedFrom":makeQuery(id+"F1.opExtrude","CAP_EDGE",EDGE,{"disambiguationData":[OSD([sQuery(id+"F0.wireOp",EDGE,"E1.left")])],"isStart":true})}),-1.0]])]});
            var Q2;
            Q2=makeQuery(id+"F16.imprint","IMPRINT",FACE,{"disambiguationData":[TD([[makeQuery(id+"F16.imprint","IMPRINT",EDGE,{"derivedFrom":sQuery(id+"F16.wireOp",EDGE,"E87.MirrorCS")}),-1.0]])]});
            var Q3;
            Q3=makeQuery(id+"F2.opExtrude","CAP_FACE",FACE,{"disambiguationData":[OSD([sQuery(id+"F0.wireOp",EDGE,"E12"),sQuery(id+"F0.wireOp",EDGE,"E13"),sQuery(id+"F0.wireOp",EDGE,"E14"),sQuery(id+"F0.wireOp",EDGE,"E15"),sQuery(id+"F0.wireOp",EDGE,"E17.filletArc"),sQuery(id+"F0.wireOp",EDGE,"E18.filletArc"),sQuery(id+"F0.wireOp",EDGE,"E19.filletArc"),sQuery(id+"F0.wireOp",EDGE,"E20.filletArc"),sQuery(id+"F0.wireOp",EDGE,"E25.0"),sQuery(id+"F0.wireOp",EDGE,"E25.1"),sQuery(id+"F0.wireOp",EDGE,"E25.2"),sQuery(id+"F0.wireOp",EDGE,"E25.3"),sQuery(id+"F0.wireOp",EDGE,"E25.4"),sQuery(id+"F0.wireOp",EDGE,"E25.5"),sQuery(id+"F0.wireOp",EDGE,"E25.6"),sQuery(id+"F0.wireOp",EDGE,"E25.7")])],"isStart":false});
            extrude(context, id + "F17", {"entities" : qUnion([Q0, Q1, Q2]), "endBound" : BoundingType.UP_TO_SURFACE, "endBoundEntityFace" : qUnion([Q3]), "depth" : 25.4 * mm});
        }
    });
